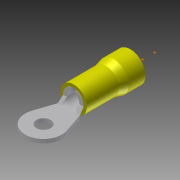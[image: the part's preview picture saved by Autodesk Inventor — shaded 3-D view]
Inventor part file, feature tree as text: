
AUTODESK INVENTOR PART (.ipt)
format: ipt  version: 2011 (Build 150239000, 239)  size: 186,880 bytes
history: native  units: mm
features: plane x2, imported_body x1, sketch x1
ambient origin geometry x8: Origin, YZ Plane, XZ Plane, XY Plane, X Axis, Y Axis, Z Axis, Center Point
bodies: Solid1 (feature_tree)
feature tree (4):
  imported_body  "Base1"
  sketch  "Sketch2"  dims[d1=3.175mm d2=3.175mm]
  plane  "Work Plane2"
  plane  "Work Plane3"
